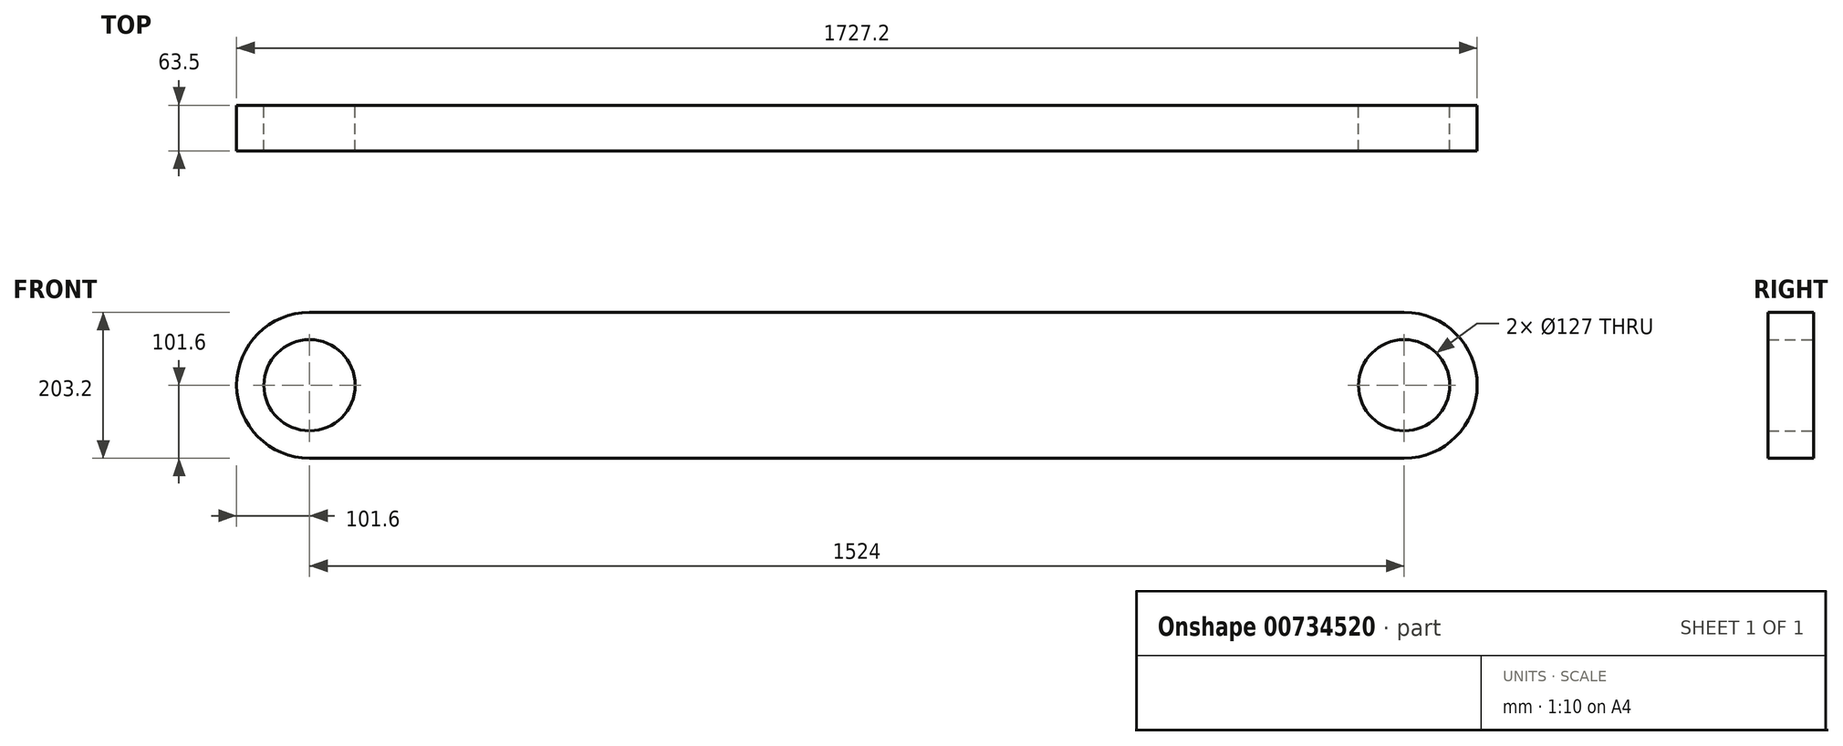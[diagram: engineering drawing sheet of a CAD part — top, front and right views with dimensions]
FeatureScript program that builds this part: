
annotation { "Feature Type Name" : "Feature", "Feature Type Description" : "" }
export const myFeature = defineFeature(function(context is Context, id is Id, definition is map)
    precondition{}
    {
        {
            var Q0;
            Q0=qCreatedBy(makeId("Front.planeOp"),FACE);
            var sketch = newSketch(context, id + "F0", { "sketchPlane" : qUnion([Q0])});
            skLineSegment(sketch, "E0", {"start": v(0, 0) * mm, "end": v(1524, 0) * mm, "construction": true});
            skArc(sketch, "E1", {"start": v(0, 101.6) * mm, "mid": v(-101.6, 0) * mm, "end": v(0, -101.6) * mm});
            skArc(sketch, "E2", {"start": v(1524, -101.6) * mm, "mid": v(1625.6, 0) * mm, "end": v(1524, 101.6) * mm});
            skLineSegment(sketch, "E3.0", {"start": v(0, -101.6) * mm, "end": v(1524, -101.6) * mm});
            skLineSegment(sketch, "E4.0", {"start": v(0, 101.6) * mm, "end": v(1524, 101.6) * mm});
            skCircle(sketch, "E5", {"center": v(0, 0) * mm, "radius": 63.5 * mm});
            skCircle(sketch, "E6", {"center": v(1524, 0) * mm, "radius": 63.5 * mm});
            skSolve(sketch);
        }
        {
            var Q0;
            Q0 = qSketchRegion(id + "F0", true);
            extrude(context, id + "F1", {"entities" : qUnion([Q0]), "depth" : 63.5 * mm, "offsetDistance" : 25.4 * mm});
        }
    });
